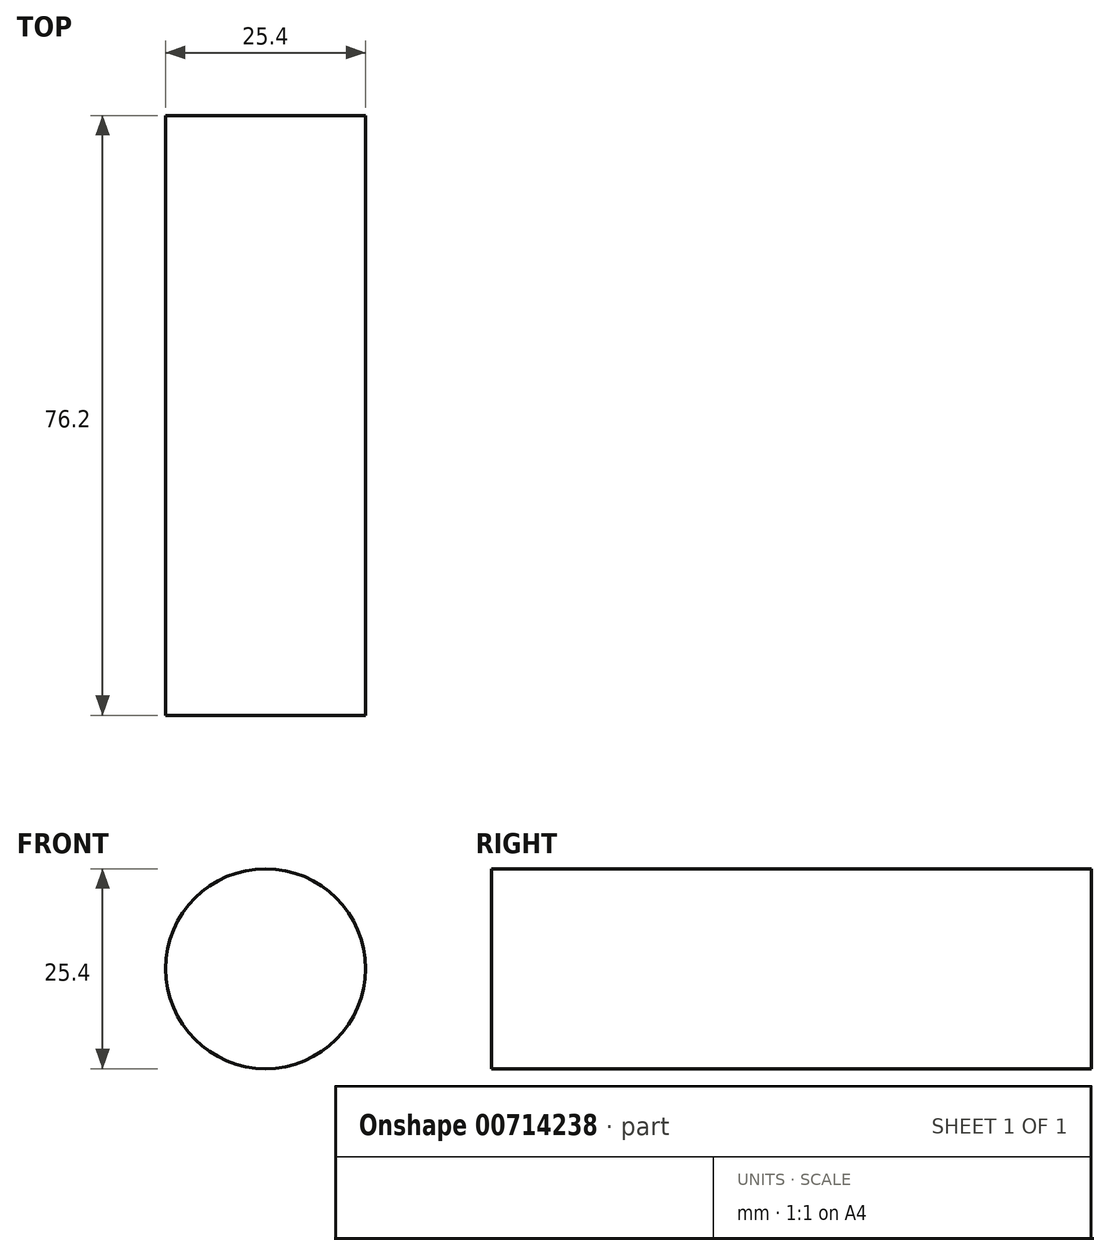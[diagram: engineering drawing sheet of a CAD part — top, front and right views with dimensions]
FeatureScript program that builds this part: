
annotation { "Feature Type Name" : "Feature", "Feature Type Description" : "" }
export const myFeature = defineFeature(function(context is Context, id is Id, definition is map)
    precondition{}
    {
        {
            var Q0;
            Q0=qCreatedBy(makeId("Front.planeOp"),FACE);
            var sketch = newSketch(context, id + "F0", { "sketchPlane" : qUnion([Q0])});
            skCircle(sketch, "E0", {"center": v(0, 0) * mm, "radius": 12.7 * mm});
            skSolve(sketch);
        }
        {
            var Q0;
            Q0=makeQuery(id+"F0.imprint","IMPRINT",FACE,{"disambiguationData":[TD([[makeQuery(id+"F0.imprint","IMPRINT",EDGE,{"derivedFrom":sQuery(id+"F0.wireOp",EDGE,"E0")}),1.0]])]});
            extrude(context, id + "F1", {"entities" : qUnion([Q0]), "depth" : 76.2 * mm, "offsetDistance" : 25.4 * mm});
        }
    });
